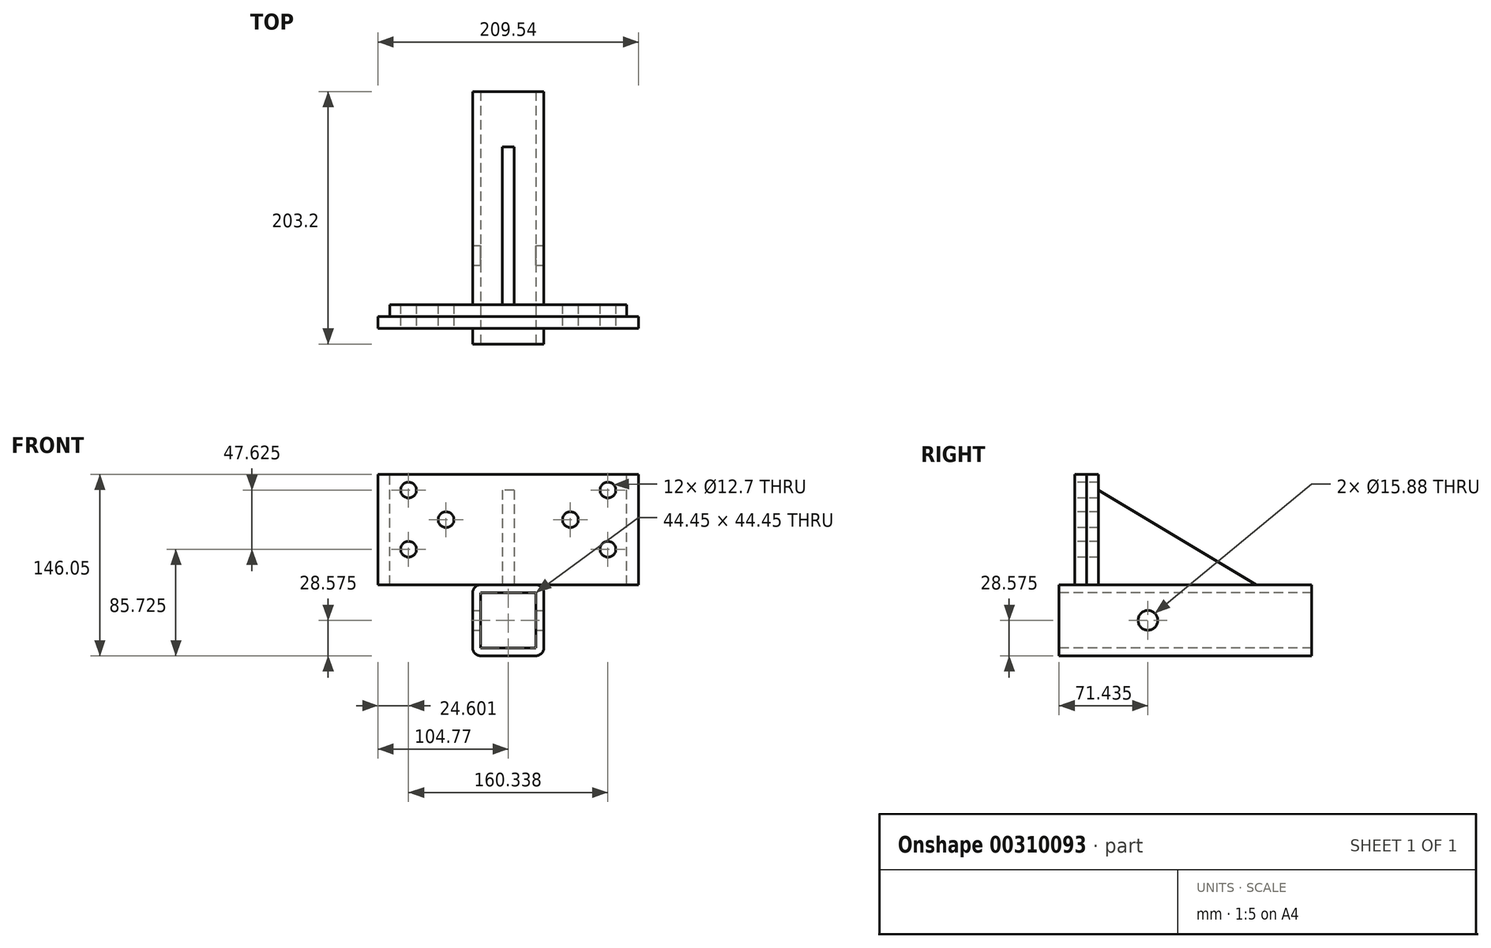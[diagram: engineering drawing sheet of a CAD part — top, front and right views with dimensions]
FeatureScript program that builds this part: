
annotation { "Feature Type Name" : "Feature", "Feature Type Description" : "" }
export const myFeature = defineFeature(function(context is Context, id is Id, definition is map)
    precondition{}
    {
        {
            var Q0;
            Q0=qCreatedBy(makeId("Front.planeOp"),FACE);
            var sketch = newSketch(context, id + "F0", { "sketchPlane" : qUnion([Q0])});
            skLineSegment(sketch, "E0.bottom", {"start": v(104.78, -44.45) * mm, "end": v(-104.78, -44.45) * mm});
            skLineSegment(sketch, "E0.top", {"start": v(104.78, 44.45) * mm, "end": v(-104.78, 44.45) * mm});
            skLineSegment(sketch, "E0.left", {"start": v(104.78, -44.45) * mm, "end": v(104.77, 44.45) * mm});
            skLineSegment(sketch, "E0.right", {"start": v(-104.78, -44.45) * mm, "end": v(-104.78, 44.45) * mm});
            skPoint(sketch, "E0.middle", {"position": v(0, 0) * mm});
            skSolve(sketch);
        }
        {
            var Q0;
            Q0=makeQuery(id+"F0.imprint","IMPRINT",FACE,{"disambiguationData":[TD([[makeQuery(id+"F0.imprint","IMPRINT",EDGE,{"derivedFrom":sQuery(id+"F0.wireOp",EDGE,"E0.bottom")}),-1.0]])]});
            extrude(context, id + "F1", {"entities" : qUnion([Q0]), "endBound" : BoundingType.SYMMETRIC, "depth" : 9.52 * mm});
        }
        {
            var Q0;
            Q0=makeQuery(id+"F1.opExtrude","CAP_FACE",FACE,{"disambiguationData":[OSD([sQuery(id+"F0.wireOp",EDGE,"E0.bottom"),sQuery(id+"F0.wireOp",EDGE,"E0.top"),sQuery(id+"F0.wireOp",EDGE,"E0.left"),sQuery(id+"F0.wireOp",EDGE,"E0.right")])],"isStart":false});
            var sketch = newSketch(context, id + "F2", { "sketchPlane" : qUnion([Q0])});
            skLineSegment(sketch, "E1.bottom", {"start": v(80.17, -15.87) * mm, "end": v(-80.17, -15.88) * mm, "construction": true});
            skLineSegment(sketch, "E1.top", {"start": v(80.17, 31.75) * mm, "end": v(-80.17, 31.75) * mm, "construction": true});
            skLineSegment(sketch, "E1.left", {"start": v(80.17, -15.88) * mm, "end": v(80.17, 31.75) * mm, "construction": true});
            skLineSegment(sketch, "E1.right", {"start": v(-80.17, -15.88) * mm, "end": v(-80.17, 31.75) * mm, "construction": true});
            skPoint(sketch, "E1.middle", {"position": v(0, 7.94) * mm});
            skLineSegment(sketch, "E2", {"start": v(-50, 7.94) * mm, "end": v(50, 7.94) * mm, "construction": true});
            skCircle(sketch, "E3", {"center": v(-80.17, 31.75) * mm, "radius": 6.35 * mm});
            skCircle(sketch, "E4", {"center": v(-50, 7.94) * mm, "radius": 6.35 * mm});
            skCircle(sketch, "E5", {"center": v(-80.17, -15.88) * mm, "radius": 6.35 * mm});
            skCircle(sketch, "E6", {"center": v(80.17, 31.75) * mm, "radius": 6.35 * mm});
            skCircle(sketch, "E7", {"center": v(50, 7.94) * mm, "radius": 6.35 * mm});
            skCircle(sketch, "E8", {"center": v(80.17, -15.88) * mm, "radius": 6.35 * mm});
            skLineSegment(sketch, "E9", {"start": v(-80.17, -15.88) * mm, "end": v(-80.17, -22.23) * mm, "construction": true});
            skLineSegment(sketch, "E10", {"start": v(-50, 7.94) * mm, "end": v(-50, 1.59) * mm, "construction": true});
            skPoint(sketch, "E11", {"position": v(-80.17, 25.4) * mm});
            skPoint(sketch, "E12", {"position": v(-50, 1.59) * mm});
            skSolve(sketch);
        }
        {
            var Q0;
            Q0 = qSketchRegion(id + "F2", true);
            extrude(context, id + "F3", {"entities" : qUnion([Q0]), "operationType" : NewBodyOperationType.REMOVE, "endBound" : BoundingType.THROUGH_ALL, "oppositeDirection" : true, "depth" : 25.4 * mm});
        }
        {
            var Q0;
            Q0=makeQuery(id+"F1.opExtrude","CAP_FACE",FACE,{"disambiguationData":[OSD([sQuery(id+"F0.wireOp",EDGE,"E0.bottom"),sQuery(id+"F0.wireOp",EDGE,"E0.top"),sQuery(id+"F0.wireOp",EDGE,"E0.left"),sQuery(id+"F0.wireOp",EDGE,"E0.right")])],"isStart":true});
            var sketch = newSketch(context, id + "F4", { "sketchPlane" : qUnion([Q0])});
            skLineSegment(sketch, "E13.bottom", {"start": v(-95.25, -44.45) * mm, "end": v(95.25, -44.45) * mm});
            skLineSegment(sketch, "E13.top", {"start": v(-95.25, 44.45) * mm, "end": v(95.25, 44.45) * mm});
            skLineSegment(sketch, "E13.left", {"start": v(-95.25, -44.45) * mm, "end": v(-95.25, 44.45) * mm});
            skLineSegment(sketch, "E13.right", {"start": v(95.25, -44.45) * mm, "end": v(95.25, 44.45) * mm});
            skPoint(sketch, "E14", {"position": v(0, -44.45) * mm});
            skCircle(sketch, "E15", {"center": v(-80.17, 31.75) * mm, "radius": 6.35 * mm});
            skCircle(sketch, "E16", {"center": v(-50, 7.94) * mm, "radius": 6.35 * mm});
            skCircle(sketch, "E17", {"center": v(-80.17, -15.88) * mm, "radius": 6.35 * mm});
            skCircle(sketch, "E18", {"center": v(50, 7.94) * mm, "radius": 6.35 * mm});
            skCircle(sketch, "E19", {"center": v(80.17, 31.75) * mm, "radius": 6.35 * mm});
            skCircle(sketch, "E20", {"center": v(80.17, -15.88) * mm, "radius": 6.35 * mm});
            skSolve(sketch);
        }
        {
            var Q0;
            Q0 = qSketchRegion(id + "F4", true);
            extrude(context, id + "F5", {"entities" : qUnion([Q0]), "depth" : 9.52 * mm});
        }
        {
            var Q0;
            Q0=makeQuery(id+"F1.opExtrude","CAP_FACE",FACE,{"disambiguationData":[OSD([sQuery(id+"F0.wireOp",EDGE,"E0.bottom"),sQuery(id+"F0.wireOp",EDGE,"E0.top"),sQuery(id+"F0.wireOp",EDGE,"E0.left"),sQuery(id+"F0.wireOp",EDGE,"E0.right")])],"isStart":false});
            cPlane(context, id + "F6", {"entities" : qUnion([Q0]), "cplaneType" : CPlaneType.OFFSET, "offset" : 12.7 * mm, "width" : 152.4 * mm, "height" : 152.4 * mm});
        }
        {
            var Q0;
            Q0=qCreatedBy(id+"F6.planeOp",FACE);
            var sketch = newSketch(context, id + "F7", { "sketchPlane" : qUnion([Q0])});
            skLineSegment(sketch, "E21.bottom", {"start": v(22.23, -101.6) * mm, "end": v(-22.22, -101.6) * mm});
            skLineSegment(sketch, "E21.top", {"start": v(22.23, -44.45) * mm, "end": v(-22.22, -44.45) * mm});
            skLineSegment(sketch, "E21.left", {"start": v(28.58, -95.25) * mm, "end": v(28.58, -50.8) * mm});
            skLineSegment(sketch, "E21.right", {"start": v(-28.57, -95.25) * mm, "end": v(-28.57, -50.8) * mm});
            skPoint(sketch, "E21.middle", {"position": v(0, -73.03) * mm});
            skPoint(sketch, "E22.visualSharp", {"position": v(-28.57, -44.45) * mm});
            skArc(sketch, "E22.filletArc", {"start": v(-22.22, -44.45) * mm, "mid": v(-26.72, -46.3) * mm, "end": v(-28.57, -50.8) * mm});
            skPoint(sketch, "E23.visualSharp", {"position": v(28.58, -44.45) * mm});
            skArc(sketch, "E23.filletArc", {"start": v(28.58, -50.8) * mm, "mid": v(26.72, -46.3) * mm, "end": v(22.23, -44.45) * mm});
            skPoint(sketch, "E24.visualSharp", {"position": v(28.58, -101.6) * mm});
            skArc(sketch, "E24.filletArc", {"start": v(22.23, -101.6) * mm, "mid": v(26.72, -99.74) * mm, "end": v(28.58, -95.25) * mm});
            skPoint(sketch, "E25.visualSharp", {"position": v(-28.57, -101.6) * mm});
            skArc(sketch, "E25.filletArc", {"start": v(-28.57, -95.25) * mm, "mid": v(-26.72, -99.74) * mm, "end": v(-22.22, -101.6) * mm});
            skLineSegment(sketch, "E26.0", {"start": v(-22.22, -95.25) * mm, "end": v(-22.22, -50.8) * mm});
            skLineSegment(sketch, "E26.1", {"start": v(22.23, -95.25) * mm, "end": v(-22.22, -95.25) * mm});
            skLineSegment(sketch, "E26.2", {"start": v(22.23, -95.25) * mm, "end": v(22.23, -50.8) * mm});
            skLineSegment(sketch, "E26.3", {"start": v(22.23, -50.8) * mm, "end": v(-22.22, -50.8) * mm});
            skSolve(sketch);
        }
        {
            var Q0;
            Q0 = qSketchRegion(id + "F7", true);
            extrude(context, id + "F8", {"entities" : qUnion([Q0]), "oppositeDirection" : true, "depth" : 203.2 * mm});
        }
        {
            var Q0;
            Q0=qCreatedBy(makeId("Right.planeOp"),FACE);
            var sketch = newSketch(context, id + "F9", { "sketchPlane" : qUnion([Q0])});
            skLineSegment(sketch, "E27", {"start": v(14.29, 31.75) * mm, "end": v(141.29, -44.45) * mm});
            skLineSegment(sketch, "E28", {"start": v(141.29, -44.45) * mm, "end": v(14.29, -44.45) * mm});
            skLineSegment(sketch, "E29", {"start": v(14.29, -44.45) * mm, "end": v(14.29, 31.75) * mm});
            skSolve(sketch);
        }
        {
            var Q0;
            Q0 = qSketchRegion(id + "F9", true);
            extrude(context, id + "F10", {"entities" : qUnion([Q0]), "endBound" : BoundingType.SYMMETRIC, "depth" : 9.52 * mm});
        }
        {
            var Q0;
            Q0=makeQuery(id+"F8.opExtrude","SWEPT_FACE",FACE,{"disambiguationData":[OSD([sQuery(id+"F7.wireOp",EDGE,"E21.left")])]});
            var sketch = newSketch(context, id + "F11", { "sketchPlane" : qUnion([Q0])});
            skCircle(sketch, "E30", {"center": v(53.97, -73.03) * mm, "radius": 7.94 * mm});
            skSolve(sketch);
        }
        {
            var Q0;
            Q0 = qSketchRegion(id + "F11", true);
            extrude(context, id + "F12", {"entities" : qUnion([Q0]), "operationType" : NewBodyOperationType.REMOVE, "endBound" : BoundingType.THROUGH_ALL, "oppositeDirection" : true, "depth" : 25.4 * mm});
        }
    });
